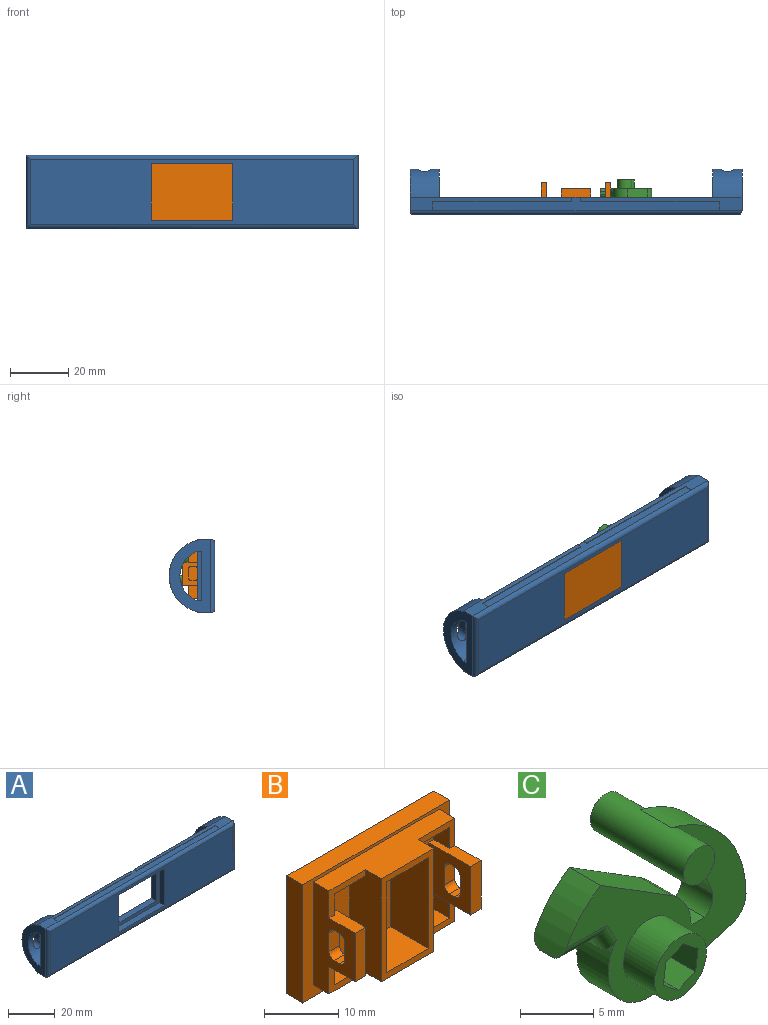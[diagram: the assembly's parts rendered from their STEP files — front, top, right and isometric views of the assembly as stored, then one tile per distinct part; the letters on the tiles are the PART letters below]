
ASSEMBLY  parts=3 mates=2
PART A: 74 faces, bbox 114x15.7x25.4 mm
  f0: plane 114x25.4mm, normal (0,1,0), area 1055.5mm2, adj f2,f3,f4,f5,f6,f7,f8,f9
  f1: plane 111x22.4mm, normal (0,-1,0), area 1940.4mm2, adj f33,f34,f35,f36,f47,f48,f49,f50
  f2: plane 24x3mm, normal (0,0,-1), area 72mm2, adj f0,f3,f5,f51
  f3: plane 17x3mm, normal (-1,0,0), area 51mm2, adj f0,f2,f4,f51
  f4: plane 24x3mm, normal (0,0,1), area 72mm2, adj f0,f3,f5,f51
  f5: plane 17x3mm, normal (1,0,0), area 51mm2, adj f0,f2,f4,f51
  f6: plane 25.4x14.2mm, normal (1,0,0), area 192.4mm2, adj f0,f8,f9,f11,f12,f34,f41,f42
  f7: plane 55.5x4.5mm, normal (0,0,1), area 106.6mm2, adj f0,f10,f25,f26,f27,f36
  f8: plane 55.5x4.5mm, normal (0,0,1), area 106.7mm2, adj f0,f6,f29,f30,f31,f36
  f9: plane 114x4.5mm, normal (0,0,-1), area 513mm2, adj f0,f6,f10,f33
  f10: plane 25.4x14.2mm, normal (-1,0,0), area 192.5mm2, adj f0,f7,f9,f14,f15,f35,f37,f38
  f11: cylinder r=9mm len=16.97mm, axis (1,0,0), area 185.3mm2, adj f6,f13,f21,f22,f23,f24,f41,f42
  f12: cylinder r=12.7mm len=24.68mm, axis (1,0,0), area 302.9mm2, adj f0,f6,f13,f21,f22,f23,f24
  f13: plane 24.68x9.7mm, normal (-1,0,0), area 103.6mm2, adj f0,f11,f12,f41,f42
  f14: cylinder r=9mm len=16.97mm, axis (-1,0,0), area 185.3mm2, adj f0,f10,f16,f17,f18,f19,f20
  f15: cylinder r=12.7mm len=24.68mm, axis (-1,0,0), area 302.9mm2, adj f0,f10,f16,f17,f18,f19,f20
  f16: plane 24.68x9.7mm, normal (1,0,0), area 103.6mm2, adj f0,f14,f15
  f17: plane 5x4.05mm, normal (1,0,0), area 18.7mm2, adj f14,f15,f18,f20
  f18: cylinder r=2.1mm len=4.72mm, axis (0,-1,0), area 26.2mm2, adj f14,f15,f17,f19
  f19: plane 5x4.05mm, normal (-1,0,0), area 18.7mm2, adj f14,f15,f18,f20
  f20: cylinder r=2.1mm len=4.72mm, axis (0,-1,0), area 26.2mm2, adj f14,f15,f17,f19
  f21: cylinder r=2.1mm len=4.72mm, axis (0,-1,0), area 26.2mm2, adj f11,f12,f22,f24
  f22: plane 5x4.05mm, normal (-1,0,0), area 18.7mm2, adj f11,f12,f21,f23
  f23: cylinder r=2.1mm len=4.72mm, axis (0,-1,0), area 26.2mm2, adj f11,f12,f22,f24
  f24: plane 5x4.05mm, normal (1,0,0), area 18.7mm2, adj f11,f12,f21,f23
  f25: plane 1.5x0.25mm, normal (1,0,0), area 0.4mm2, adj f0,f7,f26,f32
  f26: plane 47.7x0.25mm, normal (0,-1,0), area 12.1mm2, adj f7,f25,f27,f32
  f27: plane 3x0.25mm, normal (1,0,0), area 0.8mm2, adj f7,f26,f28,f32
  f28: plane 98.4x0.25mm, normal (0,1,0), area 25mm2, adj f27,f29,f32,f36
  f29: plane 3x0.25mm, normal (-1,0,0), area 0.8mm2, adj f8,f28,f30,f32
  f30: plane 47.7x0.25mm, normal (0,-1,0), area 12.1mm2, adj f8,f29,f31,f32
  f31: plane 1.5x0.25mm, normal (-1,0,0), area 0.4mm2, adj f0,f8,f30,f32
  f32: plane 98.4x4.5mm, normal (0,0,1), area 299.7mm2, adj f0,f25,f26,f27,f28,f29,f30,f31
  f33: cylinder r=1.5mm len=114mm, axis (-1,0,0), area 266mm2, adj f1,f9,f34,f35
  f34: cylinder r=1.5mm len=25.4mm, axis (0,0,1), area 57.3mm2, adj f1,f6,f33,f36
  f35: cylinder r=1.5mm len=25.4mm, axis (0,0,-1), area 57.3mm2, adj f1,f10,f33,f36
  f36: cylinder r=1.5mm len=114mm, axis (1,0,0), area 266mm2, adj f1,f7,f8,f28,f34,f35
  f37: plane 10x1.5mm, normal (0,0,-1), area 15mm2, adj f0,f10,f39,f40
  f38: plane 10x1.5mm, normal (0,0,1), area 15mm2, adj f0,f10,f39,f40
  f39: plane 16.96x10mm, normal (0,1,0), area 169.6mm2, adj f10,f37,f38,f40
  f40: plane 16.96x1.5mm, normal (-1,0,0), area 25.4mm2, adj f0,f37,f38,f39
  f41: plane 10x0.01mm, normal (0,-1,0), area 0.1mm2, adj f6,f11,f13,f45
  f42: plane 10x0.01mm, normal (0,-1,0), area 0.1mm2, adj f6,f11,f13,f43
  f43: plane 10.1x1.5mm, normal (0,0,-1), area 15.2mm2, adj f0,f6,f42,f44,f46
  f44: plane 17x10.1mm, normal (0,1,0), area 171.7mm2, adj f6,f43,f45,f46
  f45: plane 10.1x1.5mm, normal (0,0,1), area 15.2mm2, adj f0,f6,f41,f44,f46
  f46: plane 17x1.5mm, normal (1,0,0), area 25.5mm2, adj f0,f43,f44,f45
  f47: plane 28x3mm, normal (0,0,-1), area 84mm2, adj f1,f48,f50,f51
  f48: plane 19.5x3mm, normal (1,0,0), area 58.5mm2, adj f1,f47,f49,f51
  f49: plane 28x3mm, normal (0,0,1), area 84mm2, adj f1,f48,f50,f51
  f50: plane 19.5x3mm, normal (-1,0,0), area 58.5mm2, adj f1,f47,f49,f51
  f51: plane 28x19.5mm, normal (0,-1,0), area 138mm2, adj f2,f3,f4,f5,f47,f48,f49,f50
  f52: plane 8.1x3mm, normal (-1,0,0), area 24.3mm2, adj f0,f57,f58,f71
  f53: plane 3x0.5mm, normal (0,0,-1), area 1.5mm2, adj f0,f54,f58,f71
  f54: cylinder r=1.5mm len=3mm, axis (0,1,0), area 7.4mm2, adj f0,f53,f58,f73
  f55: plane 28x3mm, normal (0,0,1), area 84mm2, adj f0,f56,f58,f73
  f56: plane 17x3mm, normal (1,0,0), area 51mm2, adj f0,f55,f57,f58
  f57: plane 25x3mm, normal (0,0,-1), area 75mm2, adj f0,f52,f56,f58
  f58: plane 28x17mm, normal (0,1,0), area 448.4mm2, adj f52,f53,f54,f55,f56,f57,f71,f73
  f59: cylinder r=2.5mm len=5mm, axis (0,1,0), area 47.1mm2, adj f0,f60
  f60: plane 5x5mm, normal (0,1,0), area 19.6mm2, adj f59
  f61: plane 3x0.5mm, normal (0,0,-1), area 1.5mm2, adj f0,f66,f67,f70
  f62: plane 8.1x3mm, normal (1,0,0), area 24.3mm2, adj f0,f63,f67,f70
  f63: plane 25x3mm, normal (0,0,-1), area 75mm2, adj f0,f62,f64,f67
  f64: plane 17x3mm, normal (-1,0,0), area 51mm2, adj f0,f63,f65,f67
  f65: plane 28x3mm, normal (0,0,1), area 84mm2, adj f0,f64,f67,f72
  f66: cylinder r=1.5mm len=3mm, axis (0,1,0), area 7.4mm2, adj f0,f61,f67,f72
  f67: plane 28x17mm, normal (0,1,0), area 448.4mm2, adj f61,f62,f63,f64,f65,f66,f70,f72
  f68: cylinder r=2.5mm len=5mm, axis (0,1,0), area 47.1mm2, adj f0,f69
  f69: plane 5x5mm, normal (0,1,0), area 19.6mm2, adj f68
  f70: cylinder r=1mm len=3mm, axis (0,1,0), area 4.7mm2, adj f0,f61,f62,f67
  f71: cylinder r=1mm len=3mm, axis (0,1,0), area 4.7mm2, adj f0,f52,f53,f58
  f72: plane 6.29x3mm, normal (1,0,0), area 18.9mm2, adj f0,f65,f66,f67
  f73: plane 6.29x3mm, normal (-1,0,0), area 18.9mm2, adj f0,f54,f55,f58
PART B: 56 faces, bbox 28x11x19.5 mm
  f0: plane 7x4.5mm, normal (0,-1,0), area 10.5mm2, adj f6,f7,f8,f9,f18,f23
  f1: plane 7x4.5mm, normal (0,-1,0), area 10.5mm2, adj f11,f12,f17,f19,f20,f22
  f2: plane 7x4.5mm, normal (0,-1,0), area 10.5mm2, adj f14,f15,f16,f17,f18,f19
  f3: plane 7x4.5mm, normal (0,-1,0), area 10.5mm2, adj f4,f5,f6,f20,f21,f23
  f4: plane 3.5x3mm, normal (-1,0,0), area 10.5mm2, adj f3,f5,f21,f24
  f5: plane 6x3mm, normal (0,0,1), area 18mm2, adj f3,f4,f6,f24
  f6: plane 17x6mm, normal (1,0,0), area 96mm2, adj f0,f3,f5,f7,f18,f20,f24,f32
  f7: plane 6x3mm, normal (0,0,-1), area 18mm2, adj f0,f6,f8,f24
  f8: plane 3.5x3mm, normal (-1,0,0), area 10.5mm2, adj f0,f7,f9,f24
  f9: plane 8x2mm, normal (0,0,1), area 13mm2, adj f0,f8,f10,f23,f24,f39
  f10: plane 8x8mm, normal (-1,0,0), area 49.9mm2, adj f9,f21,f24,f39,f48,f49,f50,f51
  f11: plane 3.5x3mm, normal (1,0,0), area 10.5mm2, adj f1,f12,f22,f25
  f12: plane 8x2mm, normal (0,0,-1), area 13mm2, adj f1,f11,f13,f19,f25,f38
  f13: plane 8x8mm, normal (1,0,0), area 49.9mm2, adj f12,f14,f25,f38,f40,f41,f42,f43
  f14: plane 8x2mm, normal (0,0,1), area 13mm2, adj f2,f13,f15,f19,f25,f38
  f15: plane 3.5x3mm, normal (1,0,0), area 10.5mm2, adj f2,f14,f16,f25
  f16: plane 6x3mm, normal (0,0,-1), area 18mm2, adj f2,f15,f17,f25
  f17: plane 17x6mm, normal (-1,0,0), area 96mm2, adj f1,f2,f16,f18,f20,f22,f25,f32
  f18: plane 24x6mm, normal (0,0,1), area 102mm2, adj f0,f2,f6,f17,f19,f23,f26,f32
  f19: plane 17x8mm, normal (-1,0,0), area 76.9mm2, adj f1,f2,f12,f14,f18,f20,f26,f38
  f20: plane 24x6mm, normal (0,0,-1), area 102mm2, adj f1,f3,f6,f17,f19,f23,f26,f32
  f21: plane 8x2mm, normal (0,0,-1), area 13mm2, adj f3,f4,f10,f23,f24,f39
  f22: plane 6x3mm, normal (0,0,1), area 18mm2, adj f1,f11,f17,f25
  f23: plane 17x8mm, normal (1,0,0), area 76.9mm2, adj f0,f3,f9,f18,f20,f21,f26,f39
  f24: plane 15x6mm, normal (0,-1,0), area 82mm2, adj f4,f5,f6,f7,f8,f9,f10,f21
  f25: plane 15x6mm, normal (0,-1,0), area 82mm2, adj f11,f12,f13,f14,f15,f16,f17,f22
  f26: plane 28x19.5mm, normal (0,-1,0), area 138mm2, adj f18,f19,f20,f23,f27,f28,f29,f30
  f27: plane 28x3mm, normal (0,0,-1), area 84mm2, adj f26,f28,f30,f31
  f28: plane 19.5x3mm, normal (1,0,0), area 58.5mm2, adj f26,f27,f29,f31
  f29: plane 28x3mm, normal (0,0,1), area 84mm2, adj f26,f28,f30,f31
  f30: plane 19.5x3mm, normal (-1,0,0), area 58.5mm2, adj f26,f27,f29,f31
  f31: plane 28x19.5mm, normal (0,1,0), area 546mm2, adj f27,f28,f29,f30
  f32: plane 17x10mm, normal (0,-1,0), area 50mm2, adj f6,f17,f18,f20,f33,f34,f35,f36
  f33: plane 15x7.25mm, normal (-1,0,0), area 108.7mm2, adj f32,f34,f36,f37
  f34: plane 8x7.25mm, normal (0,0,-1), area 58mm2, adj f32,f33,f35,f37
  f35: plane 15x7.25mm, normal (1,0,0), area 108.7mm2, adj f32,f34,f36,f37
  f36: plane 8x7.25mm, normal (0,0,1), area 58mm2, adj f32,f33,f35,f37
  f37: plane 15x8mm, normal (0,-1,0), area 120mm2, adj f33,f34,f35,f36
  f38: plane 8x2mm, normal (0,-1,0), area 16mm2, adj f12,f13,f14,f19
  f39: plane 8x2mm, normal (0,-1,0), area 16mm2, adj f9,f10,f21,f23
  f40: cylinder r=1mm len=2mm, axis (-1,0,0), area 3.1mm2, adj f13,f19,f41,f47
  f41: plane 2x1mm, normal (0,0,-1), area 2mm2, adj f13,f19,f40,f42
  f42: cylinder r=1mm len=2mm, axis (-1,0,0), area 3.1mm2, adj f13,f19,f41,f43
  f43: plane 3x2mm, normal (0,-1,0), area 6mm2, adj f13,f19,f42,f44
  f44: cylinder r=1mm len=2mm, axis (-1,0,0), area 3.1mm2, adj f13,f19,f43,f45
  f45: plane 2x1mm, normal (0,0,1), area 2mm2, adj f13,f19,f44,f46
  f46: cylinder r=1mm len=2mm, axis (-1,0,0), area 3.1mm2, adj f13,f19,f45,f47
  f47: plane 3x2mm, normal (0,1,0), area 6mm2, adj f13,f19,f40,f46
  f48: cylinder r=1mm len=2mm, axis (1,0,0), area 3.1mm2, adj f10,f23,f49,f55
  f49: plane 3x2mm, normal (0,1,0), area 6mm2, adj f10,f23,f48,f50
  f50: cylinder r=1mm len=2mm, axis (1,0,0), area 3.2mm2, adj f10,f23,f49,f51
  f51: plane 2x0.98mm, normal (0,0,1), area 2mm2, adj f10,f23,f50,f52
  f52: cylinder r=1mm len=2mm, axis (1,0,0), area 3.1mm2, adj f10,f23,f51,f53
  f53: plane 3x2mm, normal (0,-1,0), area 6mm2, adj f10,f23,f52,f54
  f54: cylinder r=1mm len=2mm, axis (1,0,0), area 3.1mm2, adj f10,f23,f53,f55
  f55: plane 2x1.04mm, normal (0,0,-1), area 2.1mm2, adj f10,f23,f48,f54
PART C: 31 faces, bbox 17.8x9x13.1 mm
  f0: plane 17.32x13.04mm, normal (0,1,0), area 92.4mm2, adj f2,f5,f6,f9,f10,f11,f12,f13
  f1: plane 5x5mm, normal (0,-1,0), area 11mm2, adj f4,f22,f23,f24,f25,f26,f27
  f2: cylinder r=1.5mm len=9mm, axis (0,1,0), area 70.7mm2, adj f0,f3,f14,f15,f17,f28
  f3: plane 3x3mm, normal (0,-1,0), area 7.1mm2, adj f2
  f4: cylinder r=2.5mm len=5mm, axis (0,1,0), area 47.1mm2, adj f1,f17
  f5: plane 6.74x3mm, normal (0.27,0,-0.96), area 21mm2, adj f0,f6,f16,f17
  f6: cylinder r=4mm len=6.42mm, axis (0,-1,0), area 27mm2, adj f0,f5,f7,f17,f18,f20
  f7: plane 1.63x1mm, normal (-0.86,0,-0.51), area 1.9mm2, adj f6,f8,f18,f20
  f8: plane 3.74x1mm, normal (-0.01,0,-1), area 3.7mm2, adj f7,f9,f19,f21
  f9: cylinder r=9mm len=4.6mm, axis (0,-1,0), area 17.7mm2, adj f0,f8,f10,f17,f19,f21
  f10: plane 6.84x4.27mm, normal (0.53,0,0.85), area 24.2mm2, adj f0,f9,f11,f17
  f11: cylinder r=4mm len=3.39mm, axis (0,-1,0), area 12.1mm2, adj f0,f10,f12,f17
  f12: plane 3x1.29mm, normal (0,0,1), area 3.9mm2, adj f0,f11,f13,f17
  f13: cylinder r=1.5mm len=3mm, axis (0,-1,0), area 5.7mm2, adj f0,f12,f14,f17
  f14: cylinder r=6.29mm len=4.64mm, axis (0,-1,0), area 20.4mm2, adj f0,f2,f13,f17
  f15: cylinder r=9.29mm len=9.04mm, axis (0,-1,0), area 37.3mm2, adj f0,f2,f16,f17
  f16: cylinder r=2mm len=3mm, axis (0,-1,0), area 7.8mm2, adj f0,f5,f15,f17
  f17: plane 17.32x13.04mm, normal (0,-1,0), area 92.4mm2, adj f2,f4,f5,f6,f9,f10,f11,f12
  f18: cylinder r=1mm len=2.63mm, axis (-0.51,0,0.86), area 2.9mm2, adj f6,f7,f17,f19
  f19: cylinder r=1mm len=4.32mm, axis (-1,0,0.01), area 6mm2, adj f8,f9,f17,f18
  f20: cylinder r=1mm len=2.63mm, axis (0.51,0,-0.86), area 2.9mm2, adj f0,f6,f7,f21
  f21: cylinder r=1mm len=4.32mm, axis (1,0,-0.01), area 6mm2, adj f0,f8,f9,f20
  f22: plane 9x1.68mm, normal (-0.38,0,0.93), area 16.4mm2, adj f1,f23,f27,f30
  f23: plane 9x1.44mm, normal (0.61,0,0.79), area 16.4mm2, adj f1,f22,f24,f30
  f24: plane 9x1.8mm, normal (0.99,0,-0.13), area 16.4mm2, adj f1,f23,f25,f30
  f25: plane 9x1.68mm, normal (0.38,0,-0.93), area 16.4mm2, adj f1,f24,f26,f30
  f26: plane 9x1.44mm, normal (-0.61,0,-0.79), area 16.4mm2, adj f1,f25,f27,f30
  f27: plane 9x1.8mm, normal (-0.99,0,0.13), area 16.4mm2, adj f1,f22,f26,f30
  f28: plane 3x3mm, normal (0,1,0), area 7.1mm2, adj f2
  f29: cylinder r=2.5mm len=5mm, axis (0,-1,0), area 47.1mm2, adj f0,f30
  f30: plane 5x5mm, normal (0,1,0), area 11mm2, adj f22,f23,f24,f25,f26,f27,f29
PLACE A at identity fixed
PLACE B rot(axis=(0,0,1),180deg) t=(0,0,0.8)mm
PLACE C rot(axis=(-1,0,0),180deg) t=(0,9,1.59)mm
MATE fastened B.f26 <-> A.f51  axis (0,1,0) through (0,0,-9.7)mm
MATE revolute C.f4 <-> A.f59  axis (0,-1,0) through (16.7,3,6.3)mm
